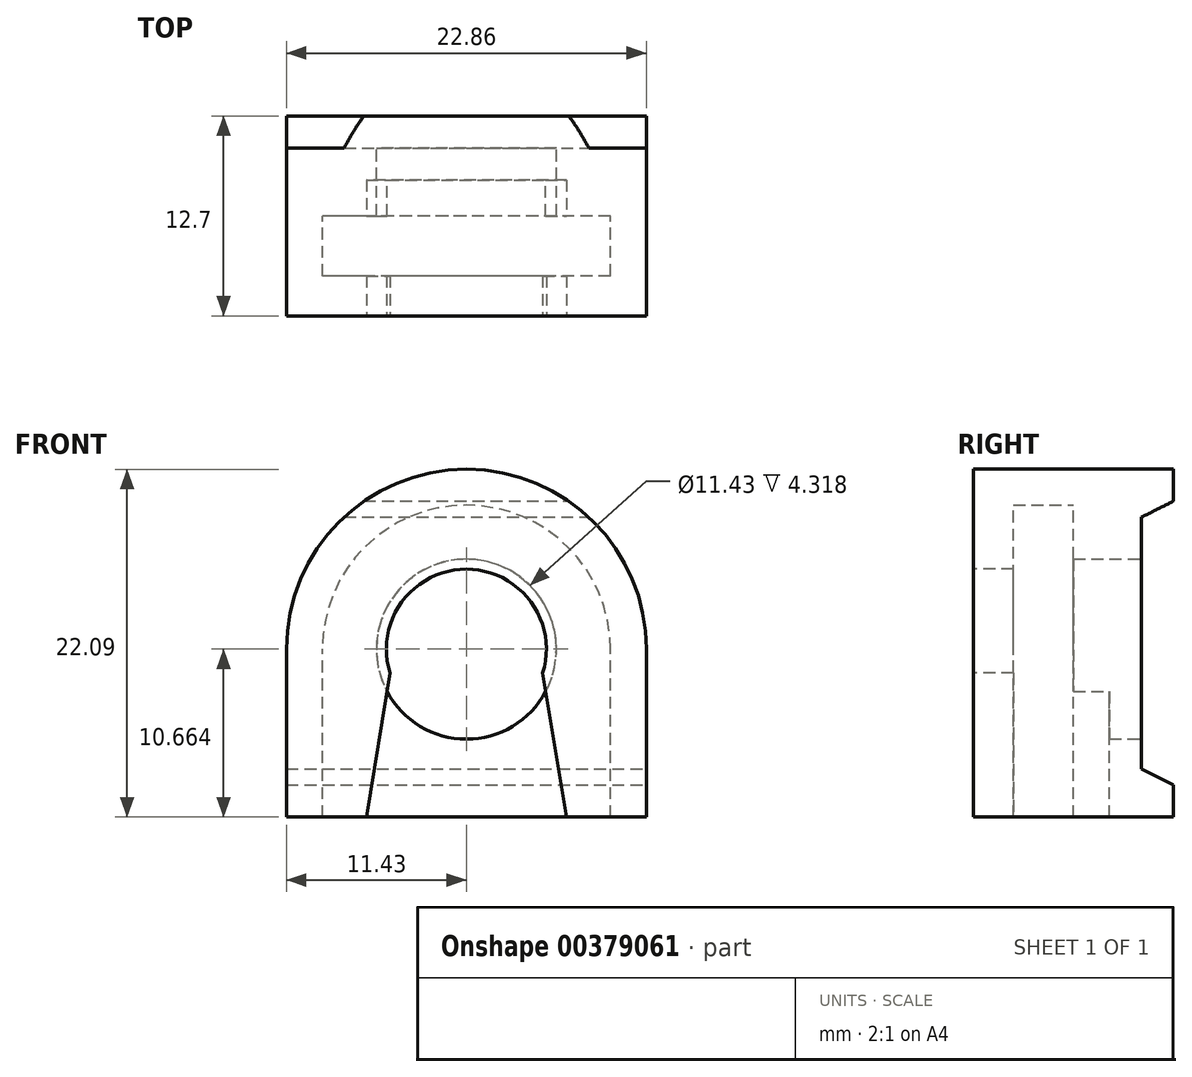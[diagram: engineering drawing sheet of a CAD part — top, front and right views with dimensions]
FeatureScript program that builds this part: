
annotation { "Feature Type Name" : "Feature", "Feature Type Description" : "" }
export const myFeature = defineFeature(function(context is Context, id is Id, definition is map)
    precondition{}
    {
        {
            var Q0;
            Q0=qCreatedBy(makeId("Front.planeOp"),FACE);
            var sketch = newSketch(context, id + "F0", { "sketchPlane" : qUnion([Q0])});
            skLineSegment(sketch, "E0.bottom", {"start": v(11.43, -5.33) * mm, "end": v(-11.43, -5.33) * mm});
            skLineSegment(sketch, "E0.left", {"start": v(11.43, -5.33) * mm, "end": v(11.43, 5.33) * mm});
            skLineSegment(sketch, "E0.right", {"start": v(-11.43, -5.33) * mm, "end": v(-11.43, 5.33) * mm});
            skPoint(sketch, "E0.middle", {"position": v(0, 0) * mm});
            skArc(sketch, "E1", {"start": v(11.43, 5.33) * mm, "mid": v(0, 16.76) * mm, "end": v(-11.43, 5.33) * mm});
            skPoint(sketch, "E2", {"position": v(0, 16.76) * mm});
            skSolve(sketch);
        }
        {
            var Q0;
            Q0 = qSketchRegion(id + "F0", true);
            extrude(context, id + "F1", {"entities" : qUnion([Q0]), "depth" : 12.7 * mm});
        }
        {
            var Q0;
            Q0=qCreatedBy(makeId("Front.planeOp"),FACE);
            cPlane(context, id + "F2", {"entities" : qUnion([Q0]), "cplaneType" : CPlaneType.OFFSET, "offset" : 6.35 * mm, "width" : 152.4 * mm, "height" : 152.4 * mm});
        }
        {
            var Q0;
            Q0=qCreatedBy(id+"F2.planeOp",FACE);
            var sketch = newSketch(context, id + "F3", { "sketchPlane" : qUnion([Q0])});
            skLineSegment(sketch, "E3.bottom", {"start": v(9.14, -5.33) * mm, "end": v(-9.14, -5.33) * mm});
            skLineSegment(sketch, "E3.left", {"start": v(9.14, -5.33) * mm, "end": v(9.14, 5.33) * mm});
            skLineSegment(sketch, "E3.right", {"start": v(-9.14, -5.33) * mm, "end": v(-9.14, 5.33) * mm});
            skLineSegment(sketch, "E4", {"start": v(0, -5.33) * mm, "end": v(0, 19.01) * mm, "construction": true});
            skArc(sketch, "E5", {"start": v(9.14, 5.33) * mm, "mid": v(0, 14.48) * mm, "end": v(-9.14, 5.33) * mm});
            skPoint(sketch, "E6", {"position": v(0, 14.48) * mm});
            skSolve(sketch);
        }
        {
            var Q0;
            Q0 = qSketchRegion(id + "F3", true);
            extrude(context, id + "F4", {"entities" : qUnion([Q0]), "operationType" : NewBodyOperationType.REMOVE, "depth" : 3.8 * mm});
        }
        {
            var Q0;
            Q0=makeQuery(id+"F1.opExtrude","CAP_FACE",FACE,{"disambiguationData":[OSD([sQuery(id+"F0.wireOp",EDGE,"E0.bottom"),sQuery(id+"F0.wireOp",EDGE,"E0.left"),sQuery(id+"F0.wireOp",EDGE,"E0.right"),sQuery(id+"F0.wireOp",EDGE,"E1")])],"isStart":false});
            var sketch = newSketch(context, id + "F5", { "sketchPlane" : qUnion([Q0])});
            skArc(sketch, "E7", {"start": v(4.85, 3.8) * mm, "mid": v(0, 10.41) * mm, "end": v(-4.85, 3.81) * mm});
            skLineSegment(sketch, "E8", {"start": v(4.85, 3.8) * mm, "end": v(-4.85, 3.8) * mm, "construction": true});
            skLineSegment(sketch, "E9", {"start": v(4.85, 3.81) * mm, "end": v(6.35, -5.33) * mm});
            skLineSegment(sketch, "E10", {"start": v(6.35, -5.33) * mm, "end": v(-6.35, -5.33) * mm});
            skLineSegment(sketch, "E11", {"start": v(-6.35, -5.33) * mm, "end": v(-4.85, 3.81) * mm});
            skLineSegment(sketch, "E12", {"start": v(0, -5.33) * mm, "end": v(0, 5.33) * mm, "construction": true});
            skSolve(sketch);
        }
        {
            var Q0;
            Q0 = qSketchRegion(id + "F5", true);
            extrude(context, id + "F6", {"entities" : qUnion([Q0]), "operationType" : NewBodyOperationType.REMOVE, "oppositeDirection" : true, "depth" : 8.64 * mm});
        }
        {
            var Q0;
            Q0=makeQuery(id+"F1.opExtrude","SWEPT_FACE",FACE,{"disambiguationData":[OSD([sQuery(id+"F0.wireOp",EDGE,"E0.left")])]});
            var sketch = newSketch(context, id + "F7", { "sketchPlane" : qUnion([Q0])});
            skLineSegment(sketch, "E13", {"start": v(0, -3.3) * mm, "end": v(-2.03, -2.29) * mm});
            skLineSegment(sketch, "E14", {"start": v(-2.03, -2.29) * mm, "end": v(-2.03, 13.72) * mm});
            skLineSegment(sketch, "E15", {"start": v(-2.03, 13.72) * mm, "end": v(0, 14.73) * mm});
            skLineSegment(sketch, "E16", {"start": v(0, 14.73) * mm, "end": v(0, -3.3) * mm});
            skLineSegment(sketch, "E17", {"start": v(-2.03, 5.71) * mm, "end": v(0, 5.71) * mm, "construction": true});
            skPoint(sketch, "E17.startSnap0", {"position": v(0, 5.71) * mm});
            skSolve(sketch);
        }
        {
            var Q0;
            Q0 = qSketchRegion(id + "F7", true);
            extrude(context, id + "F8", {"entities" : qUnion([Q0]), "operationType" : NewBodyOperationType.REMOVE, "oppositeDirection" : true, "depth" : 25.4 * mm});
        }
        {
            var Q0;
            Q0=makeQuery(id+"F8.boolean.opBoolean","COPY",FACE,{"derivedFrom":makeQuery(id+"F8.opExtrude","SWEPT_FACE",FACE,{"disambiguationData":[OSD([sQuery(id+"F7.wireOp",EDGE,"E14")])]})});
            var sketch = newSketch(context, id + "F9", { "sketchPlane" : qUnion([Q0])});
            skCircle(sketch, "E18", {"center": v(0, 5.33) * mm, "radius": 5.72 * mm});
            skSolve(sketch);
        }
        {
            var Q0;
            Q0 = qSketchRegion(id + "F9", true);
            var Q1;
            Q1=qCreatedBy(id+"F2.planeOp",FACE);
            extrude(context, id + "F10", {"entities" : qUnion([Q0]), "operationType" : NewBodyOperationType.REMOVE, "endBound" : BoundingType.UP_TO_SURFACE, "oppositeDirection" : true, "endBoundEntityFace" : qUnion([Q1]), "depth" : 25.4 * mm});
        }
    });
